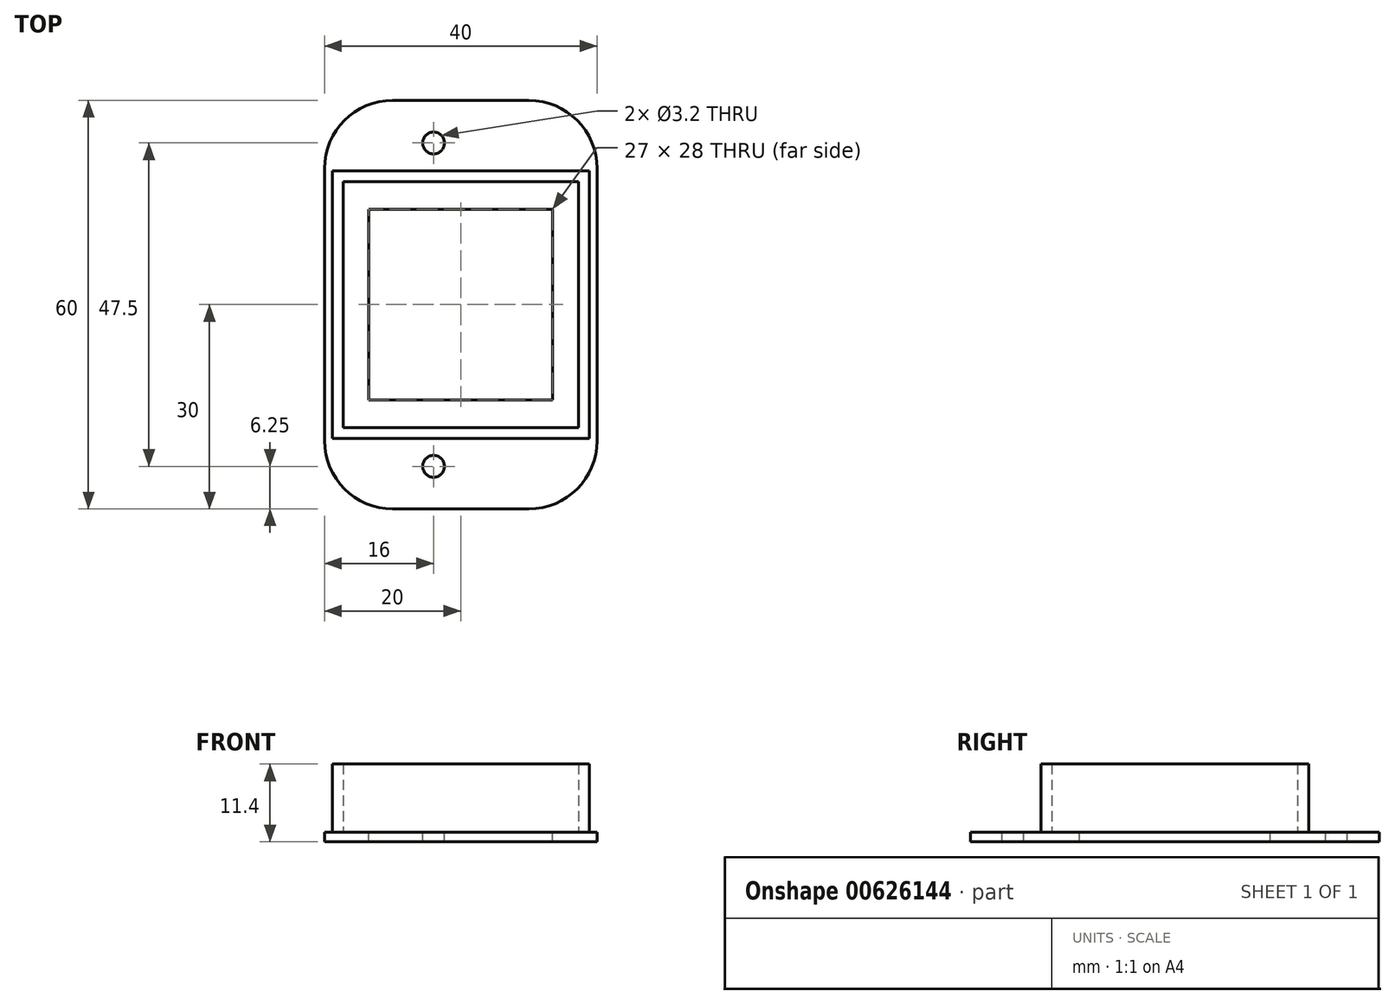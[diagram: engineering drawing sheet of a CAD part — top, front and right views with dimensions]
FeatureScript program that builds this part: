
annotation { "Feature Type Name" : "Feature", "Feature Type Description" : "" }
export const myFeature = defineFeature(function(context is Context, id is Id, definition is map)
    precondition{}
    {
        {
            var Q0;
            Q0=qCreatedBy(makeId("Top.planeOp"),FACE);
            var sketch = newSketch(context, id + "F0", { "sketchPlane" : qUnion([Q0])});
            skLineSegment(sketch, "E0.bottom", {"start": v(20, -30) * mm, "end": v(-20, -30) * mm});
            skLineSegment(sketch, "E0.top", {"start": v(20, 30) * mm, "end": v(-20, 30) * mm});
            skLineSegment(sketch, "E0.left", {"start": v(20, -30) * mm, "end": v(20, 30) * mm});
            skLineSegment(sketch, "E0.right", {"start": v(-20, -30) * mm, "end": v(-20, 30) * mm});
            skPoint(sketch, "E0.middle", {"position": v(0, 0) * mm});
            skSolve(sketch);
        }
        {
            var Q0;
            Q0 = qSketchRegion(id + "F0", true);
            extrude(context, id + "F1", {"entities" : qUnion([Q0]), "depth" : 1.4 * mm, "offsetDistance" : 25 * mm});
        }
        {
            var Q0;
            Q0=makeQuery(id+"F1.opExtrude","CAP_FACE",FACE,{"disambiguationData":[OSD([sQuery(id+"F0.wireOp",EDGE,"E0.bottom"),sQuery(id+"F0.wireOp",EDGE,"E0.top"),sQuery(id+"F0.wireOp",EDGE,"E0.left"),sQuery(id+"F0.wireOp",EDGE,"E0.right")])],"isStart":false});
            var sketch = newSketch(context, id + "F2", { "sketchPlane" : qUnion([Q0])});
            skLineSegment(sketch, "E1.bottom", {"start": v(17.25, -18.05) * mm, "end": v(-17.25, -18.05) * mm});
            skLineSegment(sketch, "E1.top", {"start": v(17.25, 18.05) * mm, "end": v(-17.25, 18.05) * mm});
            skLineSegment(sketch, "E1.left", {"start": v(17.25, -18.05) * mm, "end": v(17.25, 18.05) * mm});
            skLineSegment(sketch, "E1.right", {"start": v(-17.25, -18.05) * mm, "end": v(-17.25, 18.05) * mm});
            skPoint(sketch, "E1.middle", {"position": v(0, 0) * mm});
            skLineSegment(sketch, "E2.0", {"start": v(18.85, 19.65) * mm, "end": v(-18.85, 19.65) * mm});
            skLineSegment(sketch, "E2.1", {"start": v(18.85, -19.65) * mm, "end": v(18.85, 19.65) * mm});
            skLineSegment(sketch, "E2.2", {"start": v(18.85, -19.65) * mm, "end": v(-18.85, -19.65) * mm});
            skLineSegment(sketch, "E2.3", {"start": v(-18.85, -19.65) * mm, "end": v(-18.85, 19.65) * mm});
            skSolve(sketch);
        }
        {
            var Q0;
            Q0 = qSketchRegion(id + "F2", true);
            extrude(context, id + "F3", {"entities" : qUnion([Q0]), "operationType" : NewBodyOperationType.ADD, "depth" : 10 * mm, "offsetDistance" : 25 * mm});
        }
        {
            var Q0;
            {var subQ0=sQuery(id+"F0.wireOp",EDGE,"E0.left");var subQ1=sQuery(id+"F0.wireOp",EDGE,"E0.top");var subQ2=sQuery(id+"F0.wireOp",EDGE,"E0.right");var subQ3=sQuery(id+"F0.wireOp",EDGE,"E0.bottom");Q0=makeQuery(id+"F3.boolean.opBoolean","SPLIT",FACE,{"disambiguationData":[TD([makeQuery(id+"F1.opExtrude","SWEPT_FACE",FACE,{"disambiguationData":[OSD([subQ3])]})])],"derivedFrom":makeQuery(id+"F1.opExtrude","CAP_FACE",FACE,{"disambiguationData":[OSD([subQ3,subQ1,subQ0,subQ2])],"isStart":false})});}
            var sketch = newSketch(context, id + "F4", { "sketchPlane" : qUnion([Q0])});
            skLineSegment(sketch, "E3", {"start": v(0, 30) * mm, "end": v(0, -30) * mm, "construction": true});
            skCircle(sketch, "E4", {"center": v(-4, 23.75) * mm, "radius": 1.6 * mm});
            skCircle(sketch, "E5.MirrorC", {"center": v(-4, -23.75) * mm, "radius": 1.6 * mm});
            skLineSegment(sketch, "E6.bottom", {"start": v(13.5, -14) * mm, "end": v(-13.5, -14) * mm});
            skLineSegment(sketch, "E6.top", {"start": v(13.5, 14) * mm, "end": v(-13.5, 14) * mm});
            skLineSegment(sketch, "E6.left", {"start": v(13.5, -14) * mm, "end": v(13.5, 14) * mm});
            skLineSegment(sketch, "E6.right", {"start": v(-13.5, -14) * mm, "end": v(-13.5, 14) * mm});
            skPoint(sketch, "E6.middle", {"position": v(0, 0) * mm});
            skSolve(sketch);
        }
        {
            var Q0;
            Q0 = qSketchRegion(id + "F4", true);
            extrude(context, id + "F5", {"entities" : qUnion([Q0]), "operationType" : NewBodyOperationType.REMOVE, "endBound" : BoundingType.THROUGH_ALL, "oppositeDirection" : true, "depth" : 25 * mm, "offsetDistance" : 25 * mm});
        }
        {
            var Q0;
            Q0=makeQuery(id+"F1.opExtrude","SWEPT_EDGE",EDGE,{"disambiguationData":[OSD([sQuery(id+"F0.wireOp",EDGE,"E0.bottom"),sQuery(id+"F0.wireOp",EDGE,"E0.right")])]});
            var Q1;
            Q1=makeQuery(id+"F1.opExtrude","SWEPT_EDGE",EDGE,{"disambiguationData":[OSD([sQuery(id+"F0.wireOp",EDGE,"E0.bottom"),sQuery(id+"F0.wireOp",EDGE,"E0.left")])]});
            var Q2;
            Q2=makeQuery(id+"F1.opExtrude","SWEPT_EDGE",EDGE,{"disambiguationData":[OSD([sQuery(id+"F0.wireOp",EDGE,"E0.top"),sQuery(id+"F0.wireOp",EDGE,"E0.left")])]});
            var Q3;
            Q3=makeQuery(id+"F1.opExtrude","SWEPT_EDGE",EDGE,{"disambiguationData":[OSD([sQuery(id+"F0.wireOp",EDGE,"E0.top"),sQuery(id+"F0.wireOp",EDGE,"E0.right")])]});
            fillet(context, id + "F6", {"entities" : qUnion([Q0, Q1, Q2, Q3]), "radius" : 10 * mm, "tangentPropagation" : true, "allowEdgeOverflow" : false});
        }
    });
